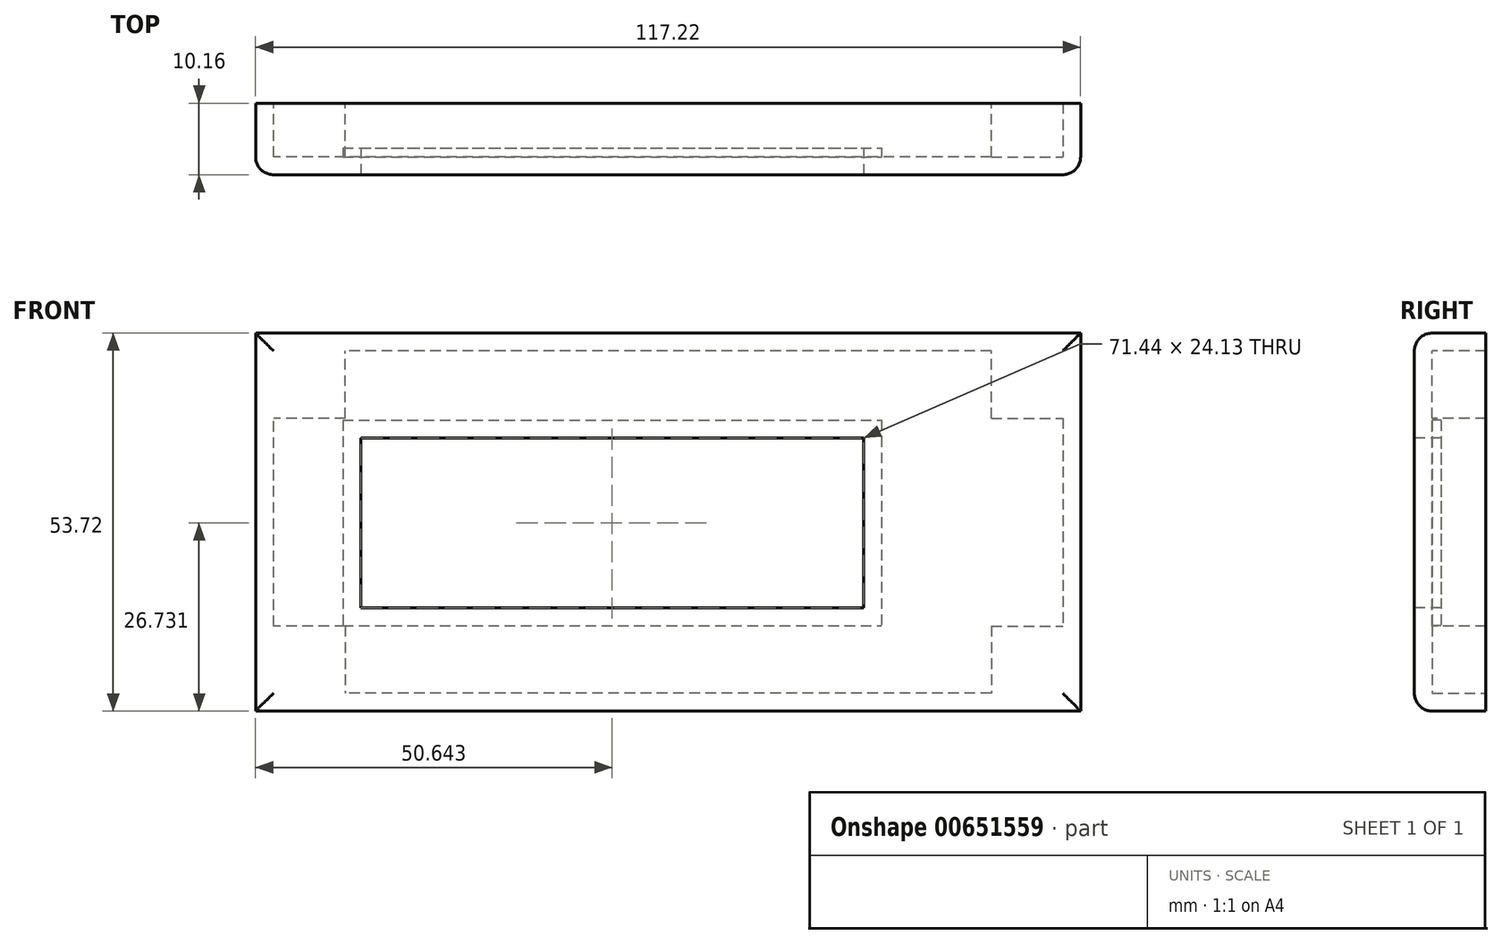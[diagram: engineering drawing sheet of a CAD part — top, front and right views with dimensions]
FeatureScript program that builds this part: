
annotation { "Feature Type Name" : "Feature", "Feature Type Description" : "" }
export const myFeature = defineFeature(function(context is Context, id is Id, definition is map)
    precondition{}
    {
        {
            var Q0;
            Q0=qCreatedBy(makeId("Front.planeOp"),FACE);
            var sketch = newSketch(context, id + "F0", { "sketchPlane" : qUnion([Q0])});
            skLineSegment(sketch, "E0.0", {"start": v(-1.59, 55.3) * mm, "end": v(-118.8, 55.3) * mm});
            skLineSegment(sketch, "E0.1", {"start": v(-1.59, 1.59) * mm, "end": v(-1.59, 55.3) * mm});
            skLineSegment(sketch, "E0.2", {"start": v(-1.59, 1.59) * mm, "end": v(-118.8, 1.59) * mm});
            skLineSegment(sketch, "E0.3", {"start": v(-118.8, 1.59) * mm, "end": v(-118.8, 55.3) * mm});
            skSolve(sketch);
        }
        {
            var Q0;
            Q0=makeQuery(id+"F0.imprint","IMPRINT",FACE,{"disambiguationData":[TD([[makeQuery(id+"F0.imprint","IMPRINT",EDGE,{"derivedFrom":sQuery(id+"F0.wireOp",EDGE,"EWna1Fgg-rQ22-0GxC-Xv1z-wVDj9juuPDVE.bottom")}),-1.0]])]});
            var Q1;
            Q1=makeQuery(id+"F0.imprint","IMPRINT",FACE,{"disambiguationData":[TD([[makeQuery(id+"F0.imprint","IMPRINT",EDGE,{"derivedFrom":sQuery(id+"F0.wireOp",EDGE,"E0.0")}),1.0]])]});
            extrude(context, id + "F1", {"entities" : qUnion([Q0, Q1]), "depth" : 10.16 * mm, "offsetDistance" : 25.4 * mm});
        }
        {
            var Q0;
            Q0=makeQuery(id+"F1.opExtrude","CAP_EDGE",EDGE,{"disambiguationData":[OSD([sQuery(id+"F0.wireOp",EDGE,"EWna1Fgg-rQ22-0GxC-Xv1z-wVDj9juuPDVE.top")])],"isStart":false});
            var Q1;
            Q1=makeQuery(id+"F1.opExtrude","CAP_EDGE",EDGE,{"disambiguationData":[OSD([sQuery(id+"F0.wireOp",EDGE,"EWna1Fgg-rQ22-0GxC-Xv1z-wVDj9juuPDVE.right")])],"isStart":false});
            var Q2;
            Q2=makeQuery(id+"F1.opExtrude","CAP_EDGE",EDGE,{"disambiguationData":[OSD([sQuery(id+"F0.wireOp",EDGE,"EWna1Fgg-rQ22-0GxC-Xv1z-wVDj9juuPDVE.bottom")])],"isStart":false});
            var Q3;
            Q3=makeQuery(id+"F1.opExtrude","CAP_EDGE",EDGE,{"disambiguationData":[OSD([sQuery(id+"F0.wireOp",EDGE,"EWna1Fgg-rQ22-0GxC-Xv1z-wVDj9juuPDVE.left")])],"isStart":false});
            var Q4;
            Q4=makeQuery(id+"F1.opExtrude","CAP_EDGE",EDGE,{"disambiguationData":[OSD([sQuery(id+"F0.wireOp",EDGE,"E0.0")])],"isStart":false});
            var Q5;
            Q5=makeQuery(id+"F1.opExtrude","CAP_EDGE",EDGE,{"disambiguationData":[OSD([sQuery(id+"F0.wireOp",EDGE,"E0.3")])],"isStart":false});
            var Q6;
            Q6=makeQuery(id+"F1.opExtrude","CAP_EDGE",EDGE,{"disambiguationData":[OSD([sQuery(id+"F0.wireOp",EDGE,"E0.2")])],"isStart":false});
            var Q7;
            Q7=makeQuery(id+"F1.opExtrude","CAP_EDGE",EDGE,{"disambiguationData":[OSD([sQuery(id+"F0.wireOp",EDGE,"E0.1")])],"isStart":false});
            fillet(context, id + "F2", {"entities" : qUnion([Q0, Q1, Q2, Q3, Q4, Q5, Q6, Q7]), "radius" : 2.54 * mm, "tangentPropagation" : true, "allowEdgeOverflow" : false});
        }
        {
            var Q0;
            Q0=makeQuery(id+"F1.opExtrude","CAP_FACE",FACE,{"disambiguationData":[OSD([sQuery(id+"F0.wireOp",EDGE,"E0.0"),sQuery(id+"F0.wireOp",EDGE,"E0.1"),sQuery(id+"F0.wireOp",EDGE,"E0.2"),sQuery(id+"F0.wireOp",EDGE,"E0.3")])],"isStart":false});
            var sketch = newSketch(context, id + "F3", { "sketchPlane" : qUnion([Q0])});
            skLineSegment(sketch, "E1.bottom", {"start": v(-103.89, 40.39) * mm, "end": v(-32.45, 40.39) * mm});
            skLineSegment(sketch, "E1.top", {"start": v(-103.89, 16.26) * mm, "end": v(-32.45, 16.26) * mm});
            skLineSegment(sketch, "E1.left", {"start": v(-103.89, 40.39) * mm, "end": v(-103.89, 16.26) * mm});
            skLineSegment(sketch, "E1.right", {"start": v(-32.45, 40.39) * mm, "end": v(-32.45, 16.26) * mm});
            skSolve(sketch);
        }
        {
            var Q0;
            Q0=makeQuery(id+"F3.imprint","IMPRINT",FACE,{"disambiguationData":[TD([[makeQuery(id+"F3.imprint","IMPRINT",EDGE,{"derivedFrom":sQuery(id+"F3.wireOp",EDGE,"E1.bottom")}),-1.0]])]});
            extrude(context, id + "F4", {"entities" : qUnion([Q0]), "operationType" : NewBodyOperationType.REMOVE, "oppositeDirection" : true, "depth" : 25.4 * mm, "offsetDistance" : 25.4 * mm});
        }
        {
            var Q0;
            Q0=makeQuery(id+"F1.opExtrude","CAP_FACE",FACE,{"disambiguationData":[OSD([sQuery(id+"F0.wireOp",EDGE,"EWna1Fgg-rQ22-0GxC-Xv1z-wVDj9juuPDVE.bottom"),sQuery(id+"F0.wireOp",EDGE,"EWna1Fgg-rQ22-0GxC-Xv1z-wVDj9juuPDVE.top"),sQuery(id+"F0.wireOp",EDGE,"EWna1Fgg-rQ22-0GxC-Xv1z-wVDj9juuPDVE.left"),sQuery(id+"F0.wireOp",EDGE,"EWna1Fgg-rQ22-0GxC-Xv1z-wVDj9juuPDVE.right")])],"isStart":true});
            var Q1;
            Q1=makeQuery(id+"F1.opExtrude","CAP_FACE",FACE,{"disambiguationData":[OSD([sQuery(id+"F0.wireOp",EDGE,"E0.0"),sQuery(id+"F0.wireOp",EDGE,"E0.1"),sQuery(id+"F0.wireOp",EDGE,"E0.2"),sQuery(id+"F0.wireOp",EDGE,"E0.3")])],"isStart":true});
            shell(context, id + "F5", {"entities" : qUnion([Q0, Q1]), "thickness" : 2.54 * mm});
        }
        {
            var Q0;
            Q0=qCreatedBy(makeId("Front.planeOp"),FACE);
            var sketch = newSketch(context, id + "F6", { "sketchPlane" : qUnion([Q0])});
            skLineSegment(sketch, "E2.top", {"start": v(-2.1, 43.2) * mm, "end": v(-14.29, 43.2) * mm});
            skLineSegment(sketch, "E2.left", {"start": v(-2.1, 54.17) * mm, "end": v(-2.1, 43.2) * mm});
            skLineSegment(sketch, "E2.right", {"start": v(-14.29, 54.17) * mm, "end": v(-14.29, 43.2) * mm});
            skLineSegment(sketch, "E3", {"start": v(0, 0) * mm, "end": v(-120.4, 56.9) * mm, "construction": true});
            skLineSegment(sketch, "E4", {"start": v(-120.4, 0) * mm, "end": v(-3.09, 55.4) * mm, "construction": true});
            skLineSegment(sketch, "E5", {"start": v(-60.17, 28.44) * mm, "end": v(39.08, 28.44) * mm, "construction": true});
            skLineSegment(sketch, "E6", {"start": v(-60.17, 28.44) * mm, "end": v(-60.17, 98.4) * mm, "construction": true});
            skLineSegment(sketch, "E7.MirrorCS", {"start": v(-118.26, 54.17) * mm, "end": v(-118.26, 43.2) * mm});
            skLineSegment(sketch, "E8.MirrorCS", {"start": v(-118.26, 43.2) * mm, "end": v(-106.06, 43.2) * mm});
            skLineSegment(sketch, "E9.MirrorCS", {"start": v(-106.06, 54.17) * mm, "end": v(-106.06, 43.2) * mm});
            skLineSegment(sketch, "E10.MirrorCS", {"start": v(-2.1, 3.35) * mm, "end": v(-2.1, 13.67) * mm});
            skLineSegment(sketch, "E11.MirrorCS", {"start": v(-2.1, 13.67) * mm, "end": v(-14.29, 13.67) * mm});
            skLineSegment(sketch, "E12.MirrorCS", {"start": v(-14.29, 3.35) * mm, "end": v(-14.29, 13.67) * mm});
            skLineSegment(sketch, "E13.MirrorCS", {"start": v(-118.26, 13.67) * mm, "end": v(-106.06, 13.67) * mm});
            skLineSegment(sketch, "E14.MirrorCS", {"start": v(-106.06, 3.35) * mm, "end": v(-106.06, 13.67) * mm});
            skLineSegment(sketch, "E15.MirrorCS", {"start": v(-118.26, 3.35) * mm, "end": v(-118.26, 13.67) * mm});
            skLineSegment(sketch, "E16", {"start": v(-2.1, 54.17) * mm, "end": v(-14.29, 54.17) * mm});
            skPoint(sketch, "E16.endSnap0", {"position": v(-118.26, 49.3) * mm});
            skLineSegment(sketch, "E17", {"start": v(-118.26, 3.35) * mm, "end": v(-106.06, 3.35) * mm});
            skPoint(sketch, "E18.orphan", {"position": v(-14.29, 1.48) * mm});
            skPoint(sketch, "E19.MirrorCS.start.orphan", {"position": v(-2.1, 1.48) * mm});
            skLineSegment(sketch, "E20.trimOffspring", {"start": v(-14.29, 3.35) * mm, "end": v(-2.1, 3.35) * mm});
            skPoint(sketch, "E21.orphan", {"position": v(-106.06, 1.48) * mm});
            skPoint(sketch, "E22.orphan", {"position": v(-118.26, 1.48) * mm});
            skPoint(sketch, "E23.orphan", {"position": v(-106.06, 55.4) * mm});
            skPoint(sketch, "E24.orphan", {"position": v(-118.26, 55.4) * mm});
            skLineSegment(sketch, "E25.trimOffspring", {"start": v(-106.06, 54.17) * mm, "end": v(-118.26, 54.17) * mm});
            skPoint(sketch, "E26.orphan", {"position": v(0, 56.85) * mm});
            skPoint(sketch, "E27.orphan", {"position": v(-2.1, 55.4) * mm});
            skPoint(sketch, "E28.orphan", {"position": v(-14.29, 55.4) * mm});
            skSolve(sketch);
        }
        {
            var Q0;
            Q0=makeQuery(id+"F6.imprint","IMPRINT",FACE,{"disambiguationData":[TD([[makeQuery(id+"F6.imprint","IMPRINT",EDGE,{"derivedFrom":sQuery(id+"F6.wireOp",EDGE,"E10.MirrorCS")}),1.0]])]});
            var Q1;
            Q1=makeQuery(id+"F6.imprint","IMPRINT",FACE,{"disambiguationData":[TD([[makeQuery(id+"F6.imprint","IMPRINT",EDGE,{"derivedFrom":sQuery(id+"F6.wireOp",EDGE,"E13.MirrorCS")}),-1.0]])]});
            var Q2;
            Q2=makeQuery(id+"F6.imprint","IMPRINT",FACE,{"disambiguationData":[TD([[makeQuery(id+"F6.imprint","IMPRINT",EDGE,{"derivedFrom":sQuery(id+"F6.wireOp",EDGE,"E7.MirrorCS")}),1.0]])]});
            var Q3;
            Q3=makeQuery(id+"F6.imprint","IMPRINT",FACE,{"disambiguationData":[TD([[makeQuery(id+"F6.imprint","IMPRINT",EDGE,{"derivedFrom":sQuery(id+"F6.wireOp",EDGE,"E2.bottom")}),1.0]])]});
            var Q4;
            Q4=makeQuery(id+"F6.imprint","IMPRINT",FACE,{"disambiguationData":[TD([[makeQuery(id+"F6.imprint","IMPRINT",EDGE,{"derivedFrom":sQuery(id+"F6.wireOp",EDGE,"E2.top")}),-1.0]])]});
            extrude(context, id + "F7", {"entities" : qUnion([Q0, Q1, Q2, Q3, Q4]), "operationType" : NewBodyOperationType.ADD, "depth" : 8.9 * mm, "offsetDistance" : 25.4 * mm});
        }
        {
            var Q0;
            Q0=makeQuery(id+"F1.opExtrude","CAP_FACE",FACE,{"disambiguationData":[OSD([sQuery(id+"F0.wireOp",EDGE,"E0.0"),sQuery(id+"F0.wireOp",EDGE,"E0.1"),sQuery(id+"F0.wireOp",EDGE,"E0.2"),sQuery(id+"F0.wireOp",EDGE,"E0.3")])],"isStart":true});
            extrude(context, id + "F8", {"entities" : qUnion([Q0]), "operationType" : NewBodyOperationType.REMOVE, "oppositeDirection" : true, "depth" : 6.35 * mm, "offsetDistance" : 25.4 * mm});
        }
    });
